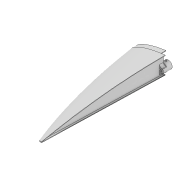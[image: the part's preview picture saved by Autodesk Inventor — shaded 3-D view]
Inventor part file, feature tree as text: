
AUTODESK INVENTOR PART (.ipt)
format: ipt  version: 2022 (Build 260153000, 153)  size: 912,896 bytes
history: native  units: mm
features: sketch x9, extrude x8, plane x4, projected_geometry x2, loft x1, shell x1, fillet x1, mirror x1
ambient origin geometry x8: Origin, YZ Plane, XZ Plane, XY Plane, X Axis, Y Axis, Z Axis, Center Point
bodies: Solid5 (feature_tree)
feature tree (27):
  plane  "Work Plane7"
  sketch  "Sketch3"  dims[d45=-250.0mm d46=70.0mm d47=1.0mm d48=5.0mm]
  plane  "Work Plane6"
  sketch  "Sketch17"  dims[d68=0.0mm d69=90.0deg d70=0.0mm d71=90.0deg]
  sketch  "Sketch18"  dims[d72=0.0mm d73=90.0deg d74=0.0mm d75=90.0deg]
  plane  "Work Plane8"
  loft  "Loft4"
  shell  "Shell3"  Thickness=5.0mm
  plane  "Work Plane10"
  sketch  "Sketch32"  dims[d104=66.0mm d122=0.5mm d123=0.0mm]
  extrude  "Extrusion19"  TaperAngle=0.0deg  [1 undecoded]
  extrude  "Extrusion20"  TaperAngle=0.0deg  [1 undecoded]
  sketch  "Sketch36"  dims[d124=0.5mm d125=0.0mm d135=9.8mm]
  extrude  "Extrusion24"  Depth=1.0mm
  extrude  "Extrusion25"  Depth=0.5mm TaperAngle=0.0deg
  extrude  "Extrusion26"  Depth=9.8mm
  extrude  "Extrusion27"  Depth=12.2mm
  extrude  "Extrusion28"  Depth=1.0mm TaperAngle=0.0deg
  fillet  "Fillet4"  Radius=1.5mm
  extrude  "Extrusion31"  Depth=10.0mm TaperAngle=0.0deg
  mirror  "Mirror1"
  sketch  "Sketch19"  dims[d76=0.0mm d77=90.0deg d78=1.0mm]
  sketch  "Sketch37"  dims[d136=4.15mm d137=12.2mm]
  sketch  "Sketch38"  dims[d138=2.0mm d139=1.0mm d140=0.0mm d141=1.5mm]
  sketch  "Sketch41"  dims[d142=12.0mm d143=0.0mm d144=10.0mm d145=0.0mm d146=2.1mm d147=6.0mm d148=100.0mm d149=0.0mm d152=8.0mm d153=0.0mm d154=5.0mm d158=2.3mm d159=4.3mm d160=1.15mm d170=3.0mm d171=3.0mm d172=40.0mm d173=1.0mm d174=4.0mm d175=10.0mm d176=0.0mm]
  projected_geometry  "Projected Loop14"
  projected_geometry  "Project Cut Edges5"
note: 2 required parameter values undecoded (feature->parameter linkage not recoverable at this tier; creation-order binding heuristic only, values carry confidence <= 0.55)
